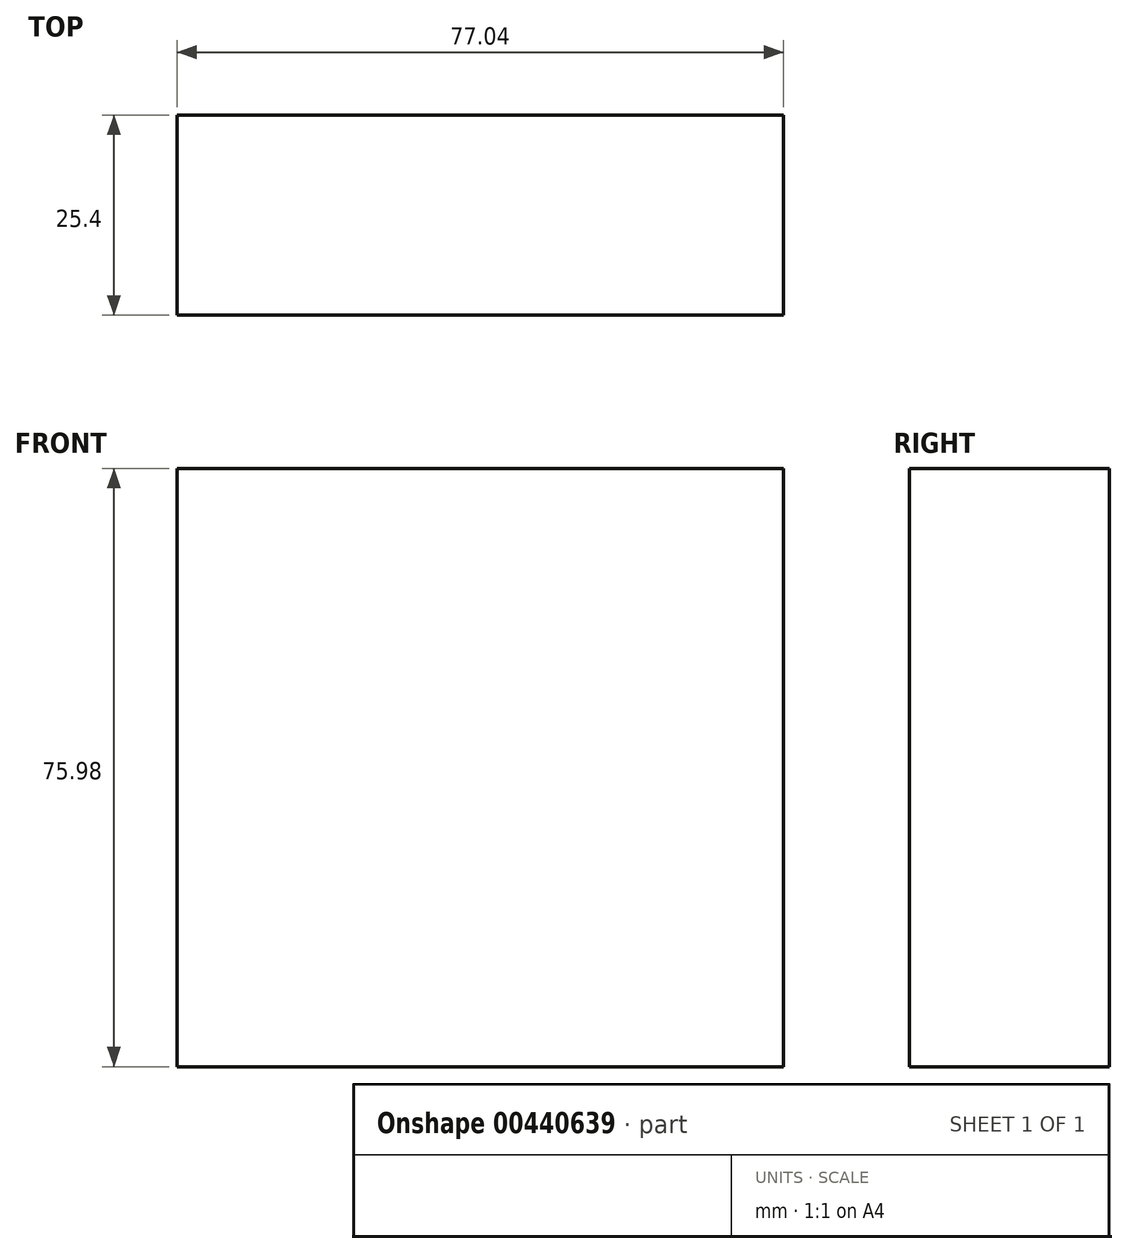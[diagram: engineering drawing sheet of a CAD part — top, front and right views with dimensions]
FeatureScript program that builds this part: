
annotation { "Feature Type Name" : "Feature", "Feature Type Description" : "" }
export const myFeature = defineFeature(function(context is Context, id is Id, definition is map)
    precondition{}
    {
        {
            var Q0;
            Q0=qCreatedBy(makeId("Front.planeOp"),FACE);
            var sketch = newSketch(context, id + "F0", { "sketchPlane" : qUnion([Q0])});
            skLineSegment(sketch, "E0.bottom", {"start": v(-40.92, 33.9) * mm, "end": v(36.12, 33.9) * mm});
            skLineSegment(sketch, "E0.top", {"start": v(-40.92, -42.07) * mm, "end": v(36.12, -42.07) * mm});
            skLineSegment(sketch, "E0.left", {"start": v(-40.92, 33.9) * mm, "end": v(-40.92, -42.07) * mm});
            skLineSegment(sketch, "E0.right", {"start": v(36.12, 33.9) * mm, "end": v(36.12, -42.07) * mm});
            skSolve(sketch);
        }
        {
            var Q0;
            Q0=makeQuery(id+"F0.imprint","IMPRINT",FACE,{"disambiguationData":[TD([[makeQuery(id+"F0.imprint","IMPRINT",EDGE,{"derivedFrom":sQuery(id+"F0.wireOp",EDGE,"E0.bottom")}),-1.0]])]});
            extrude(context, id + "F1", {"entities" : qUnion([Q0]), "depth" : 25.4 * mm});
        }
    });
